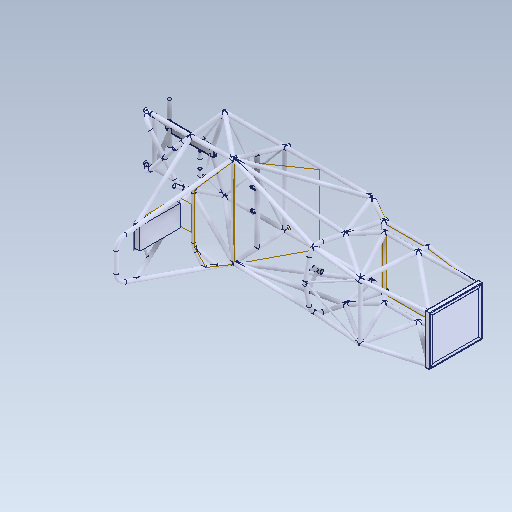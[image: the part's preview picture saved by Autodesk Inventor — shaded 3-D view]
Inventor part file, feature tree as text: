
AUTODESK INVENTOR PART (.ipt)
format: ipt  version: 2021 (Build 250183000, 183)  size: 2,537,472 bytes
history: mixed  units: in
note: dims shown in document units (in); Inventor stores cm internally (conversion verified against a paired STEP export)
features: surface_op x65, other x21, mirror x10, boolean_combine x6, imported_body x1
ambient origin geometry x8: Origin, YZ Plane, XZ Plane, XY Plane, X Axis, Y Axis, Z Axis, Center Point
bodies: Solid1 (imported_parasolid), Solid2 (imported_parasolid), Solid3 (imported_parasolid), Solid4 (imported_parasolid), Solid5 (imported_parasolid), Solid6 (imported_parasolid), Solid7 (imported_parasolid), Solid8 (imported_parasolid), Solid9 (imported_parasolid), Solid10 (imported_parasolid), Solid11 (imported_parasolid), Solid12 (imported_parasolid), Solid13 (imported_parasolid), Solid14 (imported_parasolid), Solid15 (imported_parasolid), Solid16 (imported_parasolid), Solid17 (imported_parasolid), Solid18 (imported_parasolid), Solid19 (imported_parasolid), Solid20 (imported_parasolid), Solid21 (imported_parasolid), Solid22 (imported_parasolid), Solid23 (imported_parasolid), Solid24 (imported_parasolid), Solid25 (imported_parasolid), Solid26 (imported_parasolid), Solid27 (imported_parasolid), Solid28 (imported_parasolid), Solid29 (imported_parasolid), Solid30 (imported_parasolid), Solid31 (imported_parasolid), Solid32 (imported_parasolid), Solid33 (imported_parasolid), Solid34 (imported_parasolid), Solid35 (imported_parasolid), Solid36 (imported_parasolid), Solid37 (imported_parasolid), Solid38 (imported_parasolid), Solid39 (imported_parasolid), Solid40 (imported_parasolid), Solid41 (imported_parasolid), Solid42 (imported_parasolid), Solid43 (imported_parasolid), Solid44 (imported_parasolid), Solid45 (imported_parasolid), Solid46 (imported_parasolid), Solid47 (imported_parasolid), Solid48 (imported_parasolid), Solid49 (imported_parasolid), Solid50 (imported_parasolid), Solid51 (imported_parasolid), Solid52 (imported_parasolid), Solid53 (imported_parasolid), Solid54 (imported_parasolid), Solid55 (imported_parasolid), Solid56 (imported_parasolid), Solid57 (imported_parasolid), Solid58 (imported_parasolid), Solid59 (imported_parasolid), Solid60 (imported_parasolid), Solid61 (imported_parasolid), Solid62 (imported_parasolid), Solid63 (imported_parasolid), Solid64 (imported_parasolid), Solid65 (imported_parasolid), Solid66 (imported_parasolid), Solid67 (imported_parasolid), Solid68 (imported_parasolid), Solid69 (imported_parasolid), Solid70 (imported_parasolid), Solid71 (imported_parasolid), Solid72 (imported_parasolid), Solid73 (imported_parasolid), Solid74 (imported_parasolid), Solid75 (imported_parasolid), Solid76 (imported_parasolid), Solid77 (imported_parasolid), Solid78 (imported_parasolid), Solid79 (imported_parasolid), Solid80 (imported_parasolid), Solid81 (imported_parasolid), Solid82 (imported_parasolid), Solid83 (imported_parasolid), Solid84 (imported_parasolid), Solid85 (imported_parasolid), Solid86 (imported_parasolid), Solid87 (imported_parasolid), Solid88 (imported_parasolid), Solid89 (imported_parasolid), Solid90 (imported_parasolid), Solid91 (imported_parasolid), Solid92 (imported_parasolid), Solid93 (imported_parasolid), Solid94 (imported_parasolid), Solid95 (imported_parasolid), Solid96 (imported_parasolid), Solid97 (imported_parasolid), Solid98 (imported_parasolid), Solid99 (imported_parasolid), Solid100 (imported_parasolid)
feature tree (103):
  surface_op  "Trim_Extend2"
  boolean_combine  "Combine1"
  other  "Al tube (square) 1 SQ X .049 WALL(10)[1]"
  other  "Al tube (square) 1 SQ X .049 WALL(10)[2]"
  other  "Al tube (square) 1 SQ X .049 WALL(10)[3]"
  other  "Al tube (square) 1 SQ X .049 WALL(10)[4]"
  other  "Al round tubing 1 OD X 0.049 WALL(1)[2]"
  other  "Al round tubing 1 OD X 0.049 WALL(1)[4]"
  surface_op  "Trim_Extend5[1]"
  surface_op  "Trim_Extend5[2]"
  surface_op  "Trim_Extend7[1]"
  surface_op  "Trim_Extend7[2]"
  surface_op  "Trim_Extend23[1]"
  surface_op  "Trim_Extend23[2]"
  surface_op  "Trim_Extend23[3]"
  surface_op  "Trim_Extend23[4]"
  surface_op  "Trim_Extend62[1]"
  surface_op  "Trim_Extend62[2]"
  surface_op  "Trim_Extend63[1]"
  surface_op  "Trim_Extend63[2]"
  surface_op  "Trim_Extend64[1]"
  surface_op  "Trim_Extend64[2]"
  surface_op  "Trim_Extend75[1]"
  surface_op  "Trim_Extend75[2]"
  surface_op  "Trim_Extend74[1]"
  surface_op  "Trim_Extend74[2]"
  surface_op  "Trim_Extend70[1]"
  surface_op  "Trim_Extend70[2]"
  surface_op  "Trim_Extend69[1]"
  surface_op  "Trim_Extend69[2]"
  surface_op  "Trim_Extend67"
  surface_op  "Trim_Extend76[1]"
  surface_op  "Trim_Extend76[2]"
  surface_op  "Trim_Extend79[1]"
  surface_op  "Trim_Extend79[2]"
  other  "AIP Plate -1.5mm"
  boolean_combine  "Combine3"
  surface_op  "Trim_Extend14"
  surface_op  "Trim_Extend15"
  surface_op  "Trim_Extend16[1]"
  surface_op  "Trim_Extend16[2]"
  surface_op  "Trim_Extend17[1]"
  surface_op  "Trim_Extend17[2]"
  surface_op  "Trim_Extend18[1]"
  surface_op  "Trim_Extend18[2]"
  surface_op  "Trim_Extend19[1]"
  surface_op  "Trim_Extend19[2]"
  surface_op  "Trim_Extend20[1]"
  surface_op  "Trim_Extend20[2]"
  other  "Boss-Extrude9"
  other  "Al round tubing 1.125 OD X 0.063 WALL(1)"
  surface_op  "Trim_Extend38[1]"
  surface_op  "Trim_Extend80"
  other  "Al tube (rectangular) 2.00 X 1.00 RECT X .104 WALL(18)[2]"
  surface_op  "Trim_Extend31"
  surface_op  "Trim_Extend32"
  surface_op  "Trim_Extend33"
  surface_op  "Trim_Extend30[1]"
  surface_op  "Trim_Extend30[2]"
  mirror  "Mirror1[1]"
  mirror  "Mirror1[2]"
  mirror  "Mirror1[3]"
  mirror  "Mirror1[5]"
  mirror  "Mirror1[6]"
  other  "Fsae 1 OD X 0.049 WALL(9)"
  surface_op  "Trim_Extend26"
  other  "JackbarCloseoutPlate"
  surface_op  "Trim_Extend29[1]"
  surface_op  "Trim_Extend29[2]"
  boolean_combine  "Combine9"
  surface_op  "Trim_Extend34"
  surface_op  "Trim_Extend35[1]"
  surface_op  "Trim_Extend35[2]"
  mirror  "Mirror2[1]"
  mirror  "Mirror2[2]"
  mirror  "Mirror2[3]"
  surface_op  "Trim_Extend41"
  surface_op  "Trim_Extend43[1]"
  surface_op  "Trim_Extend43[2]"
  surface_op  "Trim_Extend42[1]"
  surface_op  "Trim_Extend42[2]"
  surface_op  "Trim_Extend36"
  other  "Headrest"
  surface_op  "Trim_Extend37[1]"
  surface_op  "Trim_Extend37[2]"
  surface_op  "Trim_Extend37[3]"
  other  "Boss-Extrude6"
  surface_op  "Trim_Extend53"
  mirror  "Mirror3"
  other  "Boss-Extrude8"
  mirror  "Mirror5"
  surface_op  "Trim_Extend49[1]"
  surface_op  "Trim_Extend49[2]"
  other  "Split2[3]"
  other  "Split3[2]"
  boolean_combine  "Combine10"
  boolean_combine  "Combine11"
  boolean_combine  "Combine12"
  other  "Move Face1"
  other  "Move Face2"
  other  "Composite1"
  other  "Srf1"
  imported_body  NMx_Import_Brep_tag  [imported B-rep: ~205 faces, bbox_mm=None]
